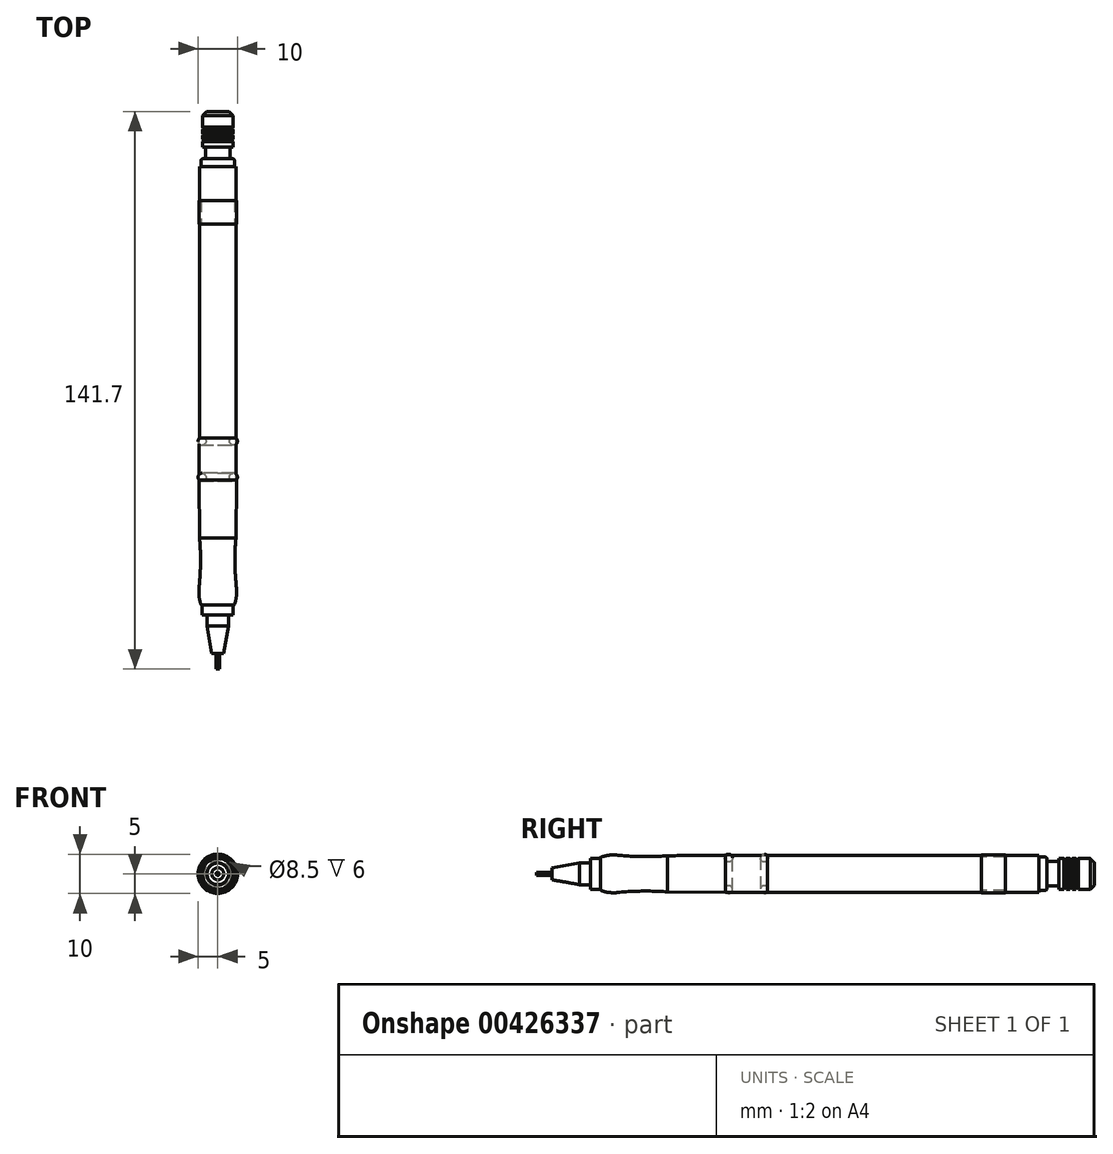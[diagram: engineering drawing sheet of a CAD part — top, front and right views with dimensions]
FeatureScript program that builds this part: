
annotation { "Feature Type Name" : "Feature", "Feature Type Description" : "" }
export const myFeature = defineFeature(function(context is Context, id is Id, definition is map)
    precondition{}
    {
        {
            var Q0;
            Q0=qCreatedBy(makeId("Front.planeOp"),FACE);
            var sketch = newSketch(context, id + "F0", { "sketchPlane" : qUnion([Q0])});
            skCircle(sketch, "E0", {"center": v(0, 0) * mm, "radius": 4.65 * mm});
            skSolve(sketch);
        }
        {
            var Q0;
            Q0 = qSketchRegion(id + "F0", true);
            extrude(context, id + "F1", {"entities" : qUnion([Q0]), "depth" : 69 * mm});
        }
        {
            var Q0;
            Q0=makeQuery(id+"F1.opExtrude","CAP_FACE",FACE,{"disambiguationData":[OSD([sQuery(id+"F0.wireOp",EDGE,"E0")])],"isStart":false});
            var sketch = newSketch(context, id + "F2", { "sketchPlane" : qUnion([Q0])});
            skCircle(sketch, "E1", {"center": v(0, 0) * mm, "radius": 4.7 * mm});
            skSolve(sketch);
        }
        {
            var Q0;
            Q0 = qSketchRegion(id + "F2", true);
            extrude(context, id + "F3", {"entities" : qUnion([Q0]), "depth" : 10.7 * mm});
        }
        {
            var Q0;
            Q0=qCreatedBy(makeId("Right.planeOp"),FACE);
            var sketch = newSketch(context, id + "F4", { "sketchPlane" : qUnion([Q0])});
            skLineSegment(sketch, "E2", {"start": v(-79.7, 0) * mm, "end": v(-111.45, 0) * mm});
            skLineSegment(sketch, "E3", {"start": v(-79.7, 0) * mm, "end": v(-79.7, 4.75) * mm});
            skLineSegment(sketch, "E4", {"start": v(-111.45, 0) * mm, "end": v(-111.45, 4.2) * mm});
            skArc(sketch, "E5", {"start": v(-107.1, 4.75) * mm, "mid": v(-109.3, 4.72) * mm, "end": v(-111.45, 4.2) * mm});
            skLineSegment(sketch, "E6", {"start": v(-79.7, 4.75) * mm, "end": v(-94.4, 4.6) * mm});
            skArc(sketch, "E7", {"start": v(-107.1, 4.75) * mm, "mid": v(-100.75, 4.38) * mm, "end": v(-94.4, 4.6) * mm});
            skSolve(sketch);
        }
        {
            var Q0;
            Q0 = qSketchRegion(id + "F4", true);
            var Q1;
            Q1=makeQuery(id+"F3.opExtrude","CAP_EDGE",EDGE,{"disambiguationData":[OSD([sQuery(id+"F2.wireOp",EDGE,"E1")])],"isStart":false});
            revolve(context, id + "F5", {"entities" : qUnion([Q0]), "axis" : qUnion([Q1]), "revolveType" : RevolveType.FULL});
        }
        {
            var Q0;
            Q0=makeQuery(id+"F5.opRevolve","SWEPT_FACE",FACE,{"disambiguationData":[OSD([sQuery(id+"F4.wireOp",EDGE,"E4")])]});
            var sketch = newSketch(context, id + "F6", { "sketchPlane" : qUnion([Q0])});
            skSolve(sketch);
        }
        {
            var Q0;
            Q0=qCreatedBy(makeId("Right.planeOp"),FACE);
            var sketch = newSketch(context, id + "F7", { "sketchPlane" : qUnion([Q0])});
            skCircle(sketch, "E8", {"center": v(-78.9, 4) * mm, "radius": 1 * mm});
            skCircle(sketch, "E9", {"center": v(-69.8, 4) * mm, "radius": 1 * mm});
            skSolve(sketch);
        }
        {
            var Q0;
            Q0 = qSketchRegion(id + "F7", true);
            var Q1;
            Q1=makeQuery(id+"F3.opExtrude","SWEPT_FACE",FACE,{"disambiguationData":[OSD([sQuery(id+"F2.wireOp",EDGE,"E1")])]});
            revolve(context, id + "F8", {"entities" : qUnion([Q0]), "axis" : qUnion([Q1]), "revolveType" : RevolveType.FULL});
        }
        {
            var Q0;
            Q0=makeQuery(id+"F6.imprint","IMPRINT",FACE,{"disambiguationData":[TD([[makeQuery(id+"F6.imprint","IMPRINT",EDGE,{"derivedFrom":makeQuery(id+"F5.opRevolve","SWEPT_EDGE",EDGE,{"disambiguationData":[OSD([sQuery(id+"F4.wireOp",EDGE,"E4"),sQuery(id+"F4.wireOp",EDGE,"E5")])]})}),-1.0]])]});
            var sketch = newSketch(context, id + "F9", { "sketchPlane" : qUnion([Q0])});
            skCircle(sketch, "E10", {"center": v(0, 0) * mm, "radius": 3.95 * mm});
            skSolve(sketch);
        }
        {
            var Q0;
            Q0 = qSketchRegion(id + "F9", true);
            extrude(context, id + "F10", {"entities" : qUnion([Q0]), "depth" : 2.5 * mm});
        }
        {
            var Q0;
            Q0=makeQuery(id+"F10.opExtrude","CAP_FACE",FACE,{"disambiguationData":[OSD([sQuery(id+"F9.wireOp",EDGE,"E10")])],"isStart":false});
            var sketch = newSketch(context, id + "F11", { "sketchPlane" : qUnion([Q0])});
            skCircle(sketch, "E11", {"center": v(0, 0) * mm, "radius": 2.75 * mm});
            skSolve(sketch);
        }
        {
            var Q0;
            Q0 = qSketchRegion(id + "F11", true);
            extrude(context, id + "F12", {"entities" : qUnion([Q0]), "operationType" : NewBodyOperationType.ADD, "depth" : 2.75 * mm});
        }
        {
            var Q0;
            Q0=makeQuery(id+"F12.opExtrude","CAP_FACE",FACE,{"disambiguationData":[OSD([sQuery(id+"F11.wireOp",EDGE,"E11")])],"isStart":false});
            var sketch = newSketch(context, id + "F13", { "sketchPlane" : qUnion([Q0])});
            skCircle(sketch, "E12", {"center": v(0, 0) * mm, "radius": 2.75 * mm});
            skSolve(sketch);
        }
        {
            var Q0;
            Q0 = qSketchRegion(id + "F13", true);
            extrude(context, id + "F14", {"entities" : qUnion([Q0]), "operationType" : NewBodyOperationType.ADD, "depth" : 7 * mm, "hasDraft" : true, "draftAngle" : 10 * degree, "draftPullDirection" : true});
        }
        {
            var Q0;
            Q0=makeQuery(id+"F14.opExtrude","CAP_FACE",FACE,{"disambiguationData":[OSD([sQuery(id+"F13.wireOp",EDGE,"E12")])],"isStart":false});
            var sketch = newSketch(context, id + "F15", { "sketchPlane" : qUnion([Q0])});
            skCircle(sketch, "E13", {"center": v(0, 0) * mm, "radius": 0.41 * mm});
            skSolve(sketch);
        }
        {
            var Q0;
            Q0 = qSketchRegion(id + "F15", true);
            extrude(context, id + "F16", {"entities" : qUnion([Q0]), "operationType" : NewBodyOperationType.ADD, "depth" : 4 * mm});
        }
        {
            var Q0;
            Q0=makeQuery(id+"F1.opExtrude","CAP_FACE",FACE,{"disambiguationData":[OSD([sQuery(id+"F0.wireOp",EDGE,"E0")])],"isStart":true});
            var sketch = newSketch(context, id + "F17", { "sketchPlane" : qUnion([Q0])});
            skCircle(sketch, "E14", {"center": v(0, 0) * mm, "radius": 4.25 * mm});
            skSolve(sketch);
        }
        {
            var Q0;
            Q0 = qSketchRegion(id + "F17", true);
            extrude(context, id + "F18", {"entities" : qUnion([Q0]), "depth" : 2 * mm});
        }
        {
            var Q0;
            Q0=makeQuery(id+"F18.opExtrude","CAP_FACE",FACE,{"disambiguationData":[OSD([sQuery(id+"F17.wireOp",EDGE,"E14")])],"isStart":false});
            var sketch = newSketch(context, id + "F19", { "sketchPlane" : qUnion([Q0])});
            skCircle(sketch, "E15", {"center": v(0, 0) * mm, "radius": 3.1 * mm});
            skSolve(sketch);
        }
        {
            var Q0;
            Q0 = qSketchRegion(id + "F19", true);
            extrude(context, id + "F20", {"entities" : qUnion([Q0]), "depth" : 3 * mm});
        }
        {
            var Q0;
            Q0=makeQuery(id+"F18.opExtrude","CAP_EDGE",EDGE,{"disambiguationData":[OSD([sQuery(id+"F17.wireOp",EDGE,"E14")])],"isStart":false});
            fillet(context, id + "F21", {"entities" : qUnion([Q0]), "radius" : .5 * mm, "tangentPropagation" : true, "allowEdgeOverflow" : false});
        }
        {
            var Q0;
            Q0=makeQuery(id+"F20.opExtrude","CAP_FACE",FACE,{"disambiguationData":[OSD([sQuery(id+"F19.wireOp",EDGE,"E15")])],"isStart":false});
            var sketch = newSketch(context, id + "F22", { "sketchPlane" : qUnion([Q0])});
            skCircle(sketch, "E16", {"center": v(0, 0) * mm, "radius": 3.9 * mm});
            skSolve(sketch);
        }
        {
            var Q0;
            Q0 = qSketchRegion(id + "F22", true);
            extrude(context, id + "F23", {"entities" : qUnion([Q0]), "operationType" : NewBodyOperationType.ADD, "depth" : 9 * mm});
        }
        {
            var Q0;
            Q0=makeQuery(id+"F23.opExtrude","CAP_EDGE",EDGE,{"disambiguationData":[OSD([sQuery(id+"F22.wireOp",EDGE,"E16")])],"isStart":false});
            chamfer(context, id + "F24", {"entities" : qUnion([Q0]), "width" : 1 * mm, "tangentPropagation" : true});
        }
        {
            var Q0;
            Q0=qCreatedBy(makeId("Right.planeOp"),FACE);
            var sketch = newSketch(context, id + "F25", { "sketchPlane" : qUnion([Q0])});
            skLineSegment(sketch, "E17.bottom", {"start": v(6.5, 4.5) * mm, "end": v(6.8, 4.5) * mm});
            skLineSegment(sketch, "E17.top", {"start": v(6.5, 3.5) * mm, "end": v(6.8, 3.5) * mm});
            skLineSegment(sketch, "E17.left", {"start": v(6.5, 4.5) * mm, "end": v(6.5, 3.5) * mm});
            skLineSegment(sketch, "E17.right", {"start": v(6.8, 4.5) * mm, "end": v(6.8, 3.5) * mm});
            skLineSegment(sketch, "E18.1.0.0", {"start": v(8, 4.5) * mm, "end": v(8.3, 4.5) * mm});
            skLineSegment(sketch, "E18.1.0.1", {"start": v(8, 3.5) * mm, "end": v(8.3, 3.5) * mm});
            skLineSegment(sketch, "E18.1.0.2", {"start": v(8, 4.5) * mm, "end": v(8, 3.5) * mm});
            skLineSegment(sketch, "E18.1.0.3", {"start": v(8.3, 4.5) * mm, "end": v(8.3, 3.5) * mm});
            skLineSegment(sketch, "E18.2.0.0", {"start": v(9.5, 4.5) * mm, "end": v(9.8, 4.5) * mm});
            skLineSegment(sketch, "E18.2.0.1", {"start": v(9.5, 3.5) * mm, "end": v(9.8, 3.5) * mm});
            skLineSegment(sketch, "E18.2.0.2", {"start": v(9.5, 4.5) * mm, "end": v(9.5, 3.5) * mm});
            skLineSegment(sketch, "E18.2.0.3", {"start": v(9.8, 4.5) * mm, "end": v(9.8, 3.5) * mm});
            skLineSegment(sketch, "E18.direction1", {"start": v(6.5, 3.5) * mm, "end": v(8, 3.5) * mm, "construction": true});
            skSolve(sketch);
        }
        {
            var Q0;
            Q0 = qSketchRegion(id + "F25", true);
            var Q1;
            Q1=makeQuery(id+"F23.opExtrude","SWEPT_FACE",FACE,{"disambiguationData":[OSD([sQuery(id+"F22.wireOp",EDGE,"E16")])]});
            revolve(context, id + "F26", {"operationType" : NewBodyOperationType.REMOVE, "entities" : qUnion([Q0]), "axis" : qUnion([Q1]), "revolveType" : RevolveType.FULL, "oppositeDirection" : true});
        }
        {
            var Q0;
            Q0=makeQuery(id+"F26.boolean.opBoolean","INTERSECT",EDGE,{"derivedFrom":[makeQuery(id+"F23.opExtrude","SWEPT_FACE",FACE,{"disambiguationData":[OSD([sQuery(id+"F22.wireOp",EDGE,"E16")])]}),makeQuery(id+"F26.opRevolve","SWEPT_FACE",FACE,{"disambiguationData":[OSD([sQuery(id+"F25.wireOp",EDGE,"E17.left")])]})]});
            var Q1;
            Q1=makeQuery(id+"F26.boolean.opBoolean","INTERSECT",EDGE,{"derivedFrom":[makeQuery(id+"F23.opExtrude","SWEPT_FACE",FACE,{"disambiguationData":[OSD([sQuery(id+"F22.wireOp",EDGE,"E16")])]}),makeQuery(id+"F26.opRevolve","SWEPT_FACE",FACE,{"disambiguationData":[OSD([sQuery(id+"F25.wireOp",EDGE,"E17.right")])]})]});
            var Q2;
            Q2=makeQuery(id+"F26.boolean.opBoolean","INTERSECT",EDGE,{"derivedFrom":[makeQuery(id+"F23.opExtrude","SWEPT_FACE",FACE,{"disambiguationData":[OSD([sQuery(id+"F22.wireOp",EDGE,"E16")])]}),makeQuery(id+"F26.opRevolve","SWEPT_FACE",FACE,{"disambiguationData":[OSD([sQuery(id+"F25.wireOp",EDGE,"E18.1.0.2")])]})]});
            var Q3;
            Q3=makeQuery(id+"F26.boolean.opBoolean","INTERSECT",EDGE,{"derivedFrom":[makeQuery(id+"F23.opExtrude","SWEPT_FACE",FACE,{"disambiguationData":[OSD([sQuery(id+"F22.wireOp",EDGE,"E16")])]}),makeQuery(id+"F26.opRevolve","SWEPT_FACE",FACE,{"disambiguationData":[OSD([sQuery(id+"F25.wireOp",EDGE,"E18.1.0.3")])]})]});
            var Q4;
            Q4=makeQuery(id+"F26.boolean.opBoolean","INTERSECT",EDGE,{"derivedFrom":[makeQuery(id+"F23.opExtrude","SWEPT_FACE",FACE,{"disambiguationData":[OSD([sQuery(id+"F22.wireOp",EDGE,"E16")])]}),makeQuery(id+"F26.opRevolve","SWEPT_FACE",FACE,{"disambiguationData":[OSD([sQuery(id+"F25.wireOp",EDGE,"E18.2.0.2")])]})]});
            var Q5;
            Q5=makeQuery(id+"F26.boolean.opBoolean","INTERSECT",EDGE,{"derivedFrom":[makeQuery(id+"F23.opExtrude","SWEPT_FACE",FACE,{"disambiguationData":[OSD([sQuery(id+"F22.wireOp",EDGE,"E16")])]}),makeQuery(id+"F26.opRevolve","SWEPT_FACE",FACE,{"disambiguationData":[OSD([sQuery(id+"F25.wireOp",EDGE,"E18.2.0.3")])]})]});
            chamfer(context, id + "F27", {"entities" : qUnion([Q0, Q1, Q2, Q3, Q4, Q5]), "width" : .2 * mm, "tangentPropagation" : true});
        }
        {
            var Q0;
            Q0=qCreatedBy(makeId("Front.planeOp"),FACE);
            cPlane(context, id + "F28", {"entities" : qUnion([Q0]), "cplaneType" : CPlaneType.OFFSET, "offset" : 14.6 * mm, "width" : 150 * mm, "height" : 150 * mm});
        }
        {
            var Q0;
            Q0=qCreatedBy(id+"F28.planeOp",FACE);
            var sketch = newSketch(context, id + "F29", { "sketchPlane" : qUnion([Q0])});
            skCircle(sketch, "E19", {"center": v(0, 0) * mm, "radius": 4.25 * mm});
            skCircle(sketch, "E20", {"center": v(0, 0) * mm, "radius": 4.8 * mm});
            skSolve(sketch);
        }
        {
            var Q0;
            Q0 = qSketchRegion(id + "F29", true);
            extrude(context, id + "F30", {"entities" : qUnion([Q0]), "oppositeDirection" : true, "depth" : 6 * mm});
        }
    });
